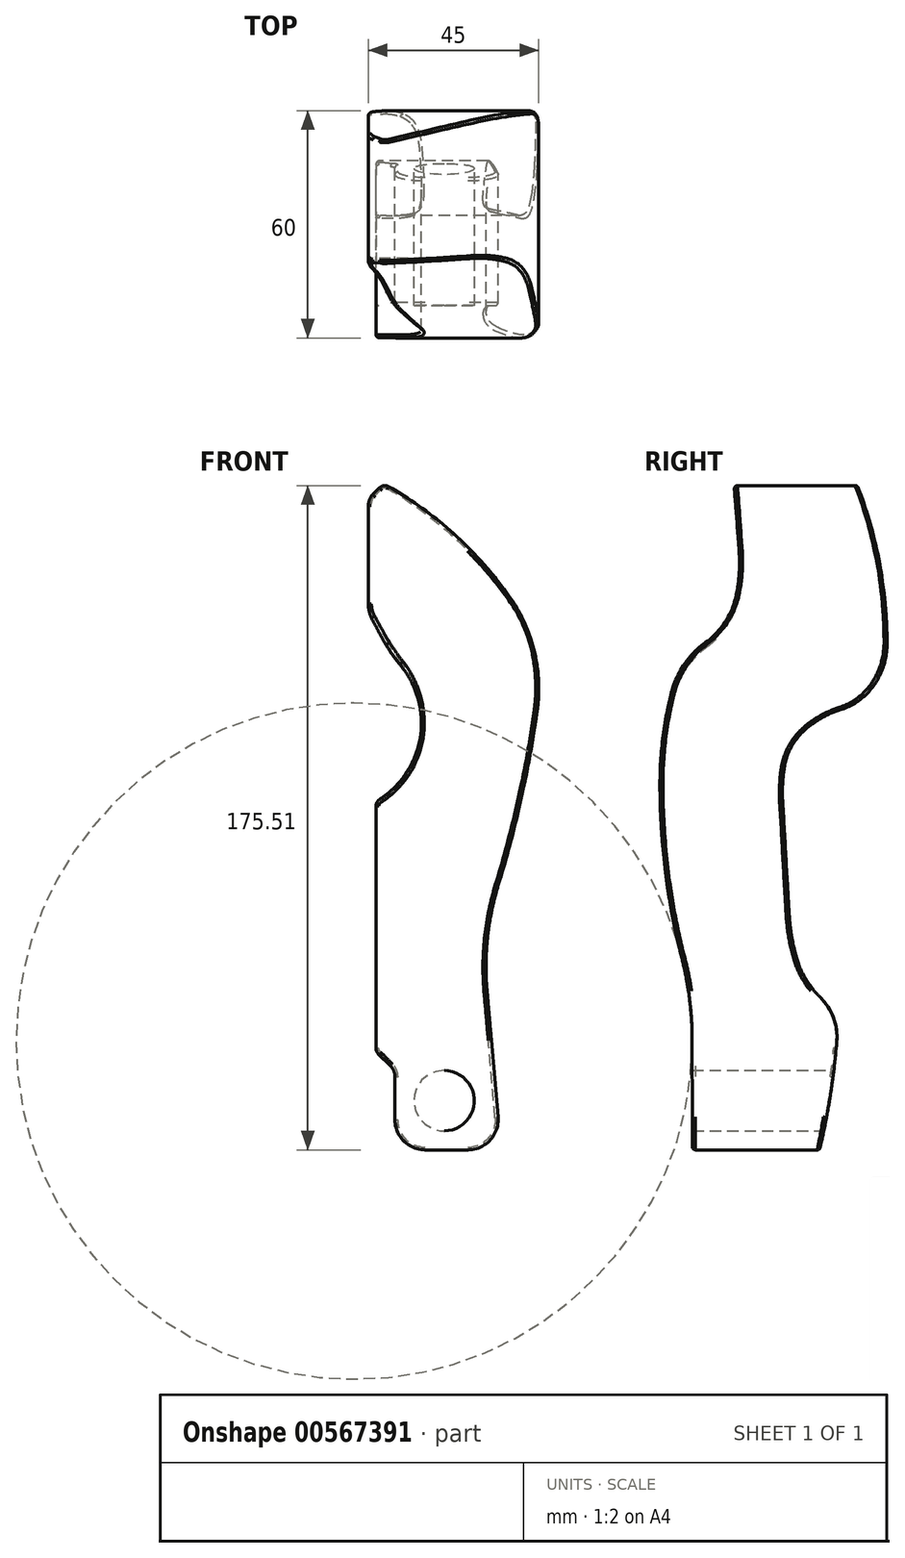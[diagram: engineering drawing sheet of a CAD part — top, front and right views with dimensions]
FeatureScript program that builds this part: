
annotation { "Feature Type Name" : "Feature", "Feature Type Description" : "" }
export const myFeature = defineFeature(function(context is Context, id is Id, definition is map)
    precondition{}
    {
        {
            var Q0;
            Q0=qCreatedBy(makeId("Front.planeOp"),FACE);
            var sketch = newSketch(context, id + "F0", { "sketchPlane" : qUnion([Q0])});
            skLineSegment(sketch, "E0", {"start": v(0, 165.13) * mm, "end": v(0, -161.9) * mm, "construction": true});
            skLineSegment(sketch, "E1", {"start": v(-141.17, 0) * mm, "end": v(180.96, 0) * mm, "construction": true});
            skLineSegment(sketch, "E2", {"start": v(5, 157.34) * mm, "end": v(5, 131) * mm});
            skLineSegment(sketch, "E3", {"start": v(5.94, 127.24) * mm, "end": v(8.2, 123) * mm});
            skLineSegment(sketch, "E4", {"start": v(7, 79) * mm, "end": v(7, 13) * mm});
            skLineSegment(sketch, "E5", {"start": v(7, 13) * mm, "end": v(12, 8) * mm});
            skLineSegment(sketch, "E6", {"start": v(12, 8) * mm, "end": v(12, -5) * mm});
            skLineSegment(sketch, "E7", {"start": v(20, -13) * mm, "end": v(31.27, -13) * mm});
            skLineSegment(sketch, "E8", {"start": v(6.17, 160.17) * mm, "end": v(7.93, 161.93) * mm});
            skArc(sketch, "E9", {"start": v(42.37, 133) * mm, "mid": v(27.96, 149.38) * mm, "end": v(10.34, 162.25) * mm});
            skLineSegment(sketch, "E10", {"start": v(39.24, -4.3) * mm, "end": v(36.33, 29) * mm});
            skArc(sketch, "E11", {"start": v(7, 79) * mm, "mid": v(18.6, 95.5) * mm, "end": v(13.52, 115) * mm});
            skCircle(sketch, "E12", {"center": v(25, 0) * mm, "radius": 8 * mm});
            skArc(sketch, "E13", {"start": v(49.59, 103) * mm, "mid": v(48.83, 118.69) * mm, "end": v(42.37, 133) * mm});
            skPoint(sketch, "E14.visualSharp", {"position": v(12, -13) * mm});
            skArc(sketch, "E14.filletArc", {"start": v(12, -5) * mm, "mid": v(14.34, -10.66) * mm, "end": v(20, -13) * mm});
            skPoint(sketch, "E15.visualSharp", {"position": v(40, -13) * mm});
            skArc(sketch, "E15.filletArc", {"start": v(31.27, -13) * mm, "mid": v(37.17, -10.4) * mm, "end": v(39.24, -4.3) * mm});
            skArc(sketch, "E16", {"start": v(36.33, 29) * mm, "mid": v(36.46, 43.14) * mm, "end": v(39.31, 57) * mm});
            skPoint(sketch, "E17.visualSharp", {"position": v(9, 163) * mm});
            skArc(sketch, "E17.filletArc", {"start": v(10.34, 162.25) * mm, "mid": v(9.08, 162.5) * mm, "end": v(7.93, 161.93) * mm});
            skPoint(sketch, "E18.visualSharp", {"position": v(5, 159) * mm});
            skArc(sketch, "E18.filletArc", {"start": v(6.17, 160.17) * mm, "mid": v(5.3, 158.87) * mm, "end": v(5, 157.34) * mm});
            skPoint(sketch, "E19.visualSharp", {"position": v(5, 129) * mm});
            skArc(sketch, "E19.filletArc", {"start": v(5, 131) * mm, "mid": v(5.24, 129.06) * mm, "end": v(5.94, 127.24) * mm});
            skArc(sketch, "E20", {"start": v(8.2, 123) * mm, "mid": v(10.66, 118.87) * mm, "end": v(13.52, 115) * mm});
            skArc(sketch, "E21", {"start": v(39.31, 57) * mm, "mid": v(45.37, 79.8) * mm, "end": v(49.59, 103) * mm});
            skSolve(sketch);
        }
        {
            var Q0;
            Q0=makeQuery(id+"F0.imprint","IMPRINT",FACE,{"disambiguationData":[TD([[makeQuery(id+"F0.imprint","IMPRINT",EDGE,{"derivedFrom":sQuery(id+"F0.wireOp",EDGE,"E2")}),1.0]])]});
            extrude(context, id + "F1", {"entities" : qUnion([Q0]), "depth" : 60 * mm, "offsetDistance" : 25 * mm, "symmetric" : true});
        }
        {
            var Q0;
            Q0=qCreatedBy(makeId("Right.planeOp"),FACE);
            var sketch = newSketch(context, id + "F2", { "sketchPlane" : qUnion([Q0])});
            skLineSegment(sketch, "E22", {"start": v(0, 199.25) * mm, "end": v(0, -40.28) * mm, "construction": true});
            skLineSegment(sketch, "E23", {"start": v(103.13, 0) * mm, "end": v(-89.2, 0) * mm, "construction": true});
            skLineSegment(sketch, "E24.0", {"start": v(30, 103) * mm, "end": v(30, 133) * mm, "construction": true});
            skLineSegment(sketch, "E25.0", {"start": v(-30, 79) * mm, "end": v(-30, 13) * mm, "construction": true});
            skLineSegment(sketch, "E26", {"start": v(-34.88, 162.51) * mm, "end": v(-10.39, 162.51) * mm});
            skLineSegment(sketch, "E27.0.1", {"start": v(36.97, -13) * mm, "end": v(12.2, -13) * mm});
            skArc(sketch, "E28", {"start": v(17.58, 103.24) * mm, "mid": v(23, 106.05) * mm, "end": v(27.08, 110.56) * mm});
            skArc(sketch, "E29", {"start": v(17.58, 103.24) * mm, "mid": v(12.26, 100.88) * mm, "end": v(7.65, 97.34) * mm});
            skArc(sketch, "E30", {"start": v(7.65, 97.34) * mm, "mid": v(4.47, 93.02) * mm, "end": v(2.83, 87.9) * mm});
            skArc(sketch, "E31", {"start": v(2.83, 87.9) * mm, "mid": v(2.4, 83.43) * mm, "end": v(2.43, 78.93) * mm});
            skLineSegment(sketch, "E32", {"start": v(2.43, 78.93) * mm, "end": v(4.14, 49.18) * mm});
            skArc(sketch, "E33", {"start": v(4.14, 49.18) * mm, "mid": v(4.76, 43.59) * mm, "end": v(5.97, 38.09) * mm});
            skArc(sketch, "E34", {"start": v(5.97, 38.09) * mm, "mid": v(8.44, 32.29) * mm, "end": v(12.33, 27.33) * mm});
            skArc(sketch, "E35", {"start": v(16.72, 15.56) * mm, "mid": v(15.85, 21.94) * mm, "end": v(12.33, 27.33) * mm});
            skArc(sketch, "E36", {"start": v(12.2, -13) * mm, "mid": v(14.97, 1.2) * mm, "end": v(16.72, 15.56) * mm});
            skArc(sketch, "E37", {"start": v(27.08, 110.56) * mm, "mid": v(29.26, 115.47) * mm, "end": v(30, 120.79) * mm});
            skArc(sketch, "E38", {"start": v(30, 120.79) * mm, "mid": v(28.02, 142.02) * mm, "end": v(22.16, 162.51) * mm});
            skLineSegment(sketch, "E39.trimOffspring", {"start": v(22.16, 162.51) * mm, "end": v(36.97, 162.51) * mm});
            skLineSegment(sketch, "E40", {"start": v(36.97, 162.51) * mm, "end": v(36.97, -13) * mm});
            skLineSegment(sketch, "E41", {"start": v(-21.42, -13) * mm, "end": v(-21.48, 15.94) * mm});
            skArc(sketch, "E42", {"start": v(-21.48, 15.94) * mm, "mid": v(-22.19, 26.94) * mm, "end": v(-24.24, 37.78) * mm});
            skArc(sketch, "E43", {"start": v(-30, 83.73) * mm, "mid": v(-28.55, 60.57) * mm, "end": v(-24.24, 37.78) * mm});
            skArc(sketch, "E44", {"start": v(-26.96, 107.8) * mm, "mid": v(-29.24, 95.86) * mm, "end": v(-30, 83.73) * mm});
            skArc(sketch, "E45", {"start": v(-17.95, 121.06) * mm, "mid": v(-23.62, 115.22) * mm, "end": v(-26.96, 107.8) * mm});
            skArc(sketch, "E46", {"start": v(-17.95, 121.06) * mm, "mid": v(-12.69, 126.63) * mm, "end": v(-9.8, 133.73) * mm});
            skArc(sketch, "E47", {"start": v(-9.8, 133.73) * mm, "mid": v(-9.05, 139.41) * mm, "end": v(-9.08, 145.15) * mm});
            skLineSegment(sketch, "E48", {"start": v(-9.08, 145.15) * mm, "end": v(-10.39, 162.51) * mm});
            skLineSegment(sketch, "E49", {"start": v(-34.88, 162.51) * mm, "end": v(-34.88, -13) * mm});
            skLineSegment(sketch, "E50.trimOffspring", {"start": v(-21.42, -13) * mm, "end": v(-34.88, -13) * mm});
            skSolve(sketch);
        }
        {
            var Q0;
            Q0=makeQuery(id+"F2.imprint","IMPRINT",FACE,{"disambiguationData":[TD([[makeQuery(id+"F2.imprint","IMPRINT",EDGE,{"derivedFrom":sQuery(id+"F2.wireOp",EDGE,"E27.0.1")}),-1.0]])]});
            var Q1;
            Q1=makeQuery(id+"F2.imprint","IMPRINT",FACE,{"disambiguationData":[TD([[makeQuery(id+"F2.imprint","IMPRINT",EDGE,{"derivedFrom":sQuery(id+"F2.wireOp",EDGE,"E26")}),-1.0]])]});
            extrude(context, id + "F3", {"entities" : qUnion([Q0, Q1]), "operationType" : NewBodyOperationType.REMOVE, "endBound" : BoundingType.THROUGH_ALL, "depth" : 25 * mm, "offsetDistance" : 25 * mm});
        }
        {
            var Q0;
            Q0=makeQuery(id+"F1.opExtrude","SWEPT_EDGE",EDGE,{"disambiguationData":[OSD([sQuery(id+"F0.wireOp",EDGE,"E4"),sQuery(id+"F0.wireOp",EDGE,"E11")])]});
            var Q1;
            Q1=makeQuery(id+"F1.opExtrude","SWEPT_EDGE",EDGE,{"disambiguationData":[OSD([sQuery(id+"F0.wireOp",EDGE,"E4"),sQuery(id+"F0.wireOp",EDGE,"E5")])]});
            fillet(context, id + "F4", {"entities" : qUnion([Q0, Q1]), "radius" : 2 * mm, "tangentPropagation" : true, "allowEdgeOverflow" : false});
        }
        {
            var Q0;
            Q0=makeQuery(id+"F1.opExtrude","SWEPT_EDGE",EDGE,{"disambiguationData":[OSD([sQuery(id+"F0.wireOp",EDGE,"E5"),sQuery(id+"F0.wireOp",EDGE,"E6")])]});
            fillet(context, id + "F5", {"entities" : qUnion([Q0]), "radius" : 4 * mm, "tangentPropagation" : true, "allowEdgeOverflow" : false});
        }
        {
            var Q0;
            Q0=makeQuery(id+"F3.boolean.opBoolean","INTERSECT",EDGE,{"derivedFrom":[makeQuery(id+"F1.opExtrude","SWEPT_FACE",FACE,{"disambiguationData":[OSD([sQuery(id+"F0.wireOp",EDGE,"E4")])]}),makeQuery(id+"F3.opExtrude","SWEPT_FACE",FACE,{"disambiguationData":[OSD([sQuery(id+"F2.wireOp",EDGE,"E43")])]})]});
            var Q1;
            Q1=makeQuery(id+"F3.boolean.opBoolean","INTERSECT",EDGE,{"derivedFrom":[makeQuery(id+"F1.opExtrude","SWEPT_FACE",FACE,{"disambiguationData":[OSD([sQuery(id+"F0.wireOp",EDGE,"E4")])]}),makeQuery(id+"F3.opExtrude","SWEPT_FACE",FACE,{"disambiguationData":[OSD([sQuery(id+"F2.wireOp",EDGE,"E32")])]})]});
            fillet(context, id + "F6", {"entities" : qUnion([Q0, Q1]), "radius" : 0.8 * mm, "tangentPropagation" : true, "allowEdgeOverflow" : false});
        }
    });
